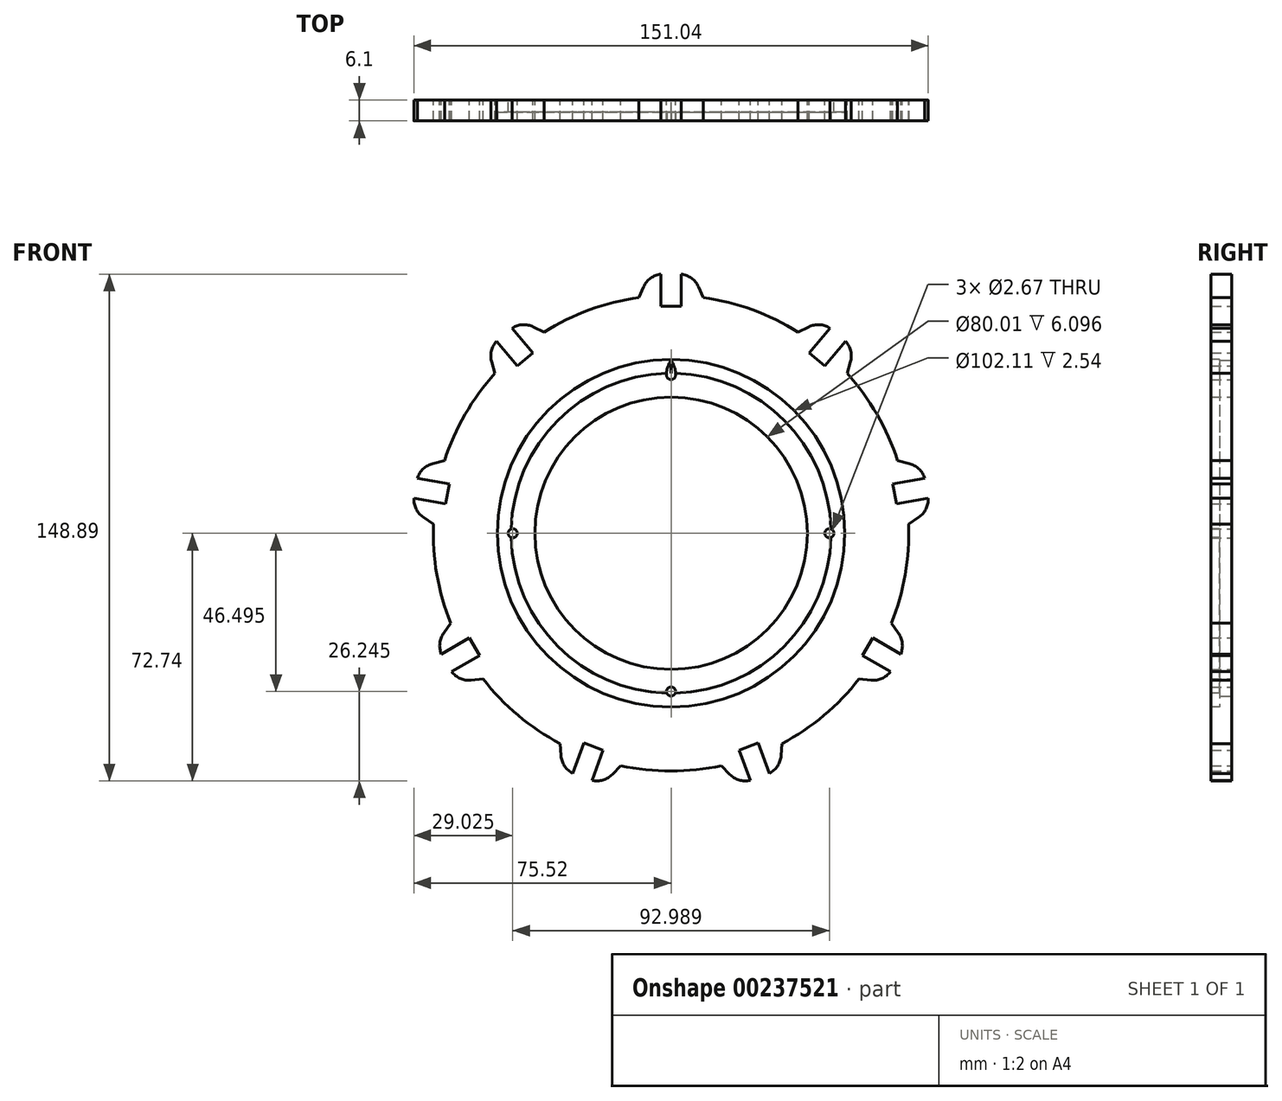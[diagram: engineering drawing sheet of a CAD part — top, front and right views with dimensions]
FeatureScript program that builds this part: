
annotation { "Feature Type Name" : "Feature", "Feature Type Description" : "" }
export const myFeature = defineFeature(function(context is Context, id is Id, definition is map)
    precondition{}
    {
        {
            var Q0;
            Q0=qCreatedBy(makeId("Front.planeOp"),FACE);
            var sketch = newSketch(context, id + "F0", { "sketchPlane" : qUnion([Q0])});
            skCircle(sketch, "E0", {"center": v(0, 0) * mm, "radius": 69.85 * mm});
            skCircle(sketch, "E1", {"center": v(0, 0) * mm, "radius": 40 * mm});
            skCircle(sketch, "E2", {"center": v(0, 0) * mm, "radius": 46.5 * mm, "construction": true});
            skPoint(sketch, "E3.center", {"position": v(0, -7.07) * mm});
            skLineSegment(sketch, "E4", {"start": v(-9.44, 69.2) * mm, "end": v(-8.02, 72.42) * mm});
            skLineSegment(sketch, "E5", {"start": v(-2.21, 76.2) * mm, "end": v(2.21, 76.2) * mm});
            skLineSegment(sketch, "E6", {"start": v(8.02, 72.42) * mm, "end": v(9.44, 69.2) * mm});
            skPoint(sketch, "E7", {"position": v(0, 76.2) * mm});
            skLineSegment(sketch, "E8", {"start": v(-9.44, 69.2) * mm, "end": v(-40, 0) * mm, "construction": true});
            skLineSegment(sketch, "E9", {"start": v(40, 0) * mm, "end": v(9.44, 69.2) * mm, "construction": true});
            skLineSegment(sketch, "E10", {"start": v(-2.98, 76.2) * mm, "end": v(-2.98, 66.67) * mm});
            skLineSegment(sketch, "E11", {"start": v(-2.98, 66.68) * mm, "end": v(2.98, 66.68) * mm});
            skLineSegment(sketch, "E12", {"start": v(2.98, 66.67) * mm, "end": v(2.98, 76.2) * mm});
            skPoint(sketch, "E13", {"position": v(0, 66.67) * mm});
            skPoint(sketch, "E14.visualSharp", {"position": v(-6.35, 76.2) * mm});
            skArc(sketch, "E14.filletArc", {"start": v(-2.21, 76.2) * mm, "mid": v(-5.68, 75.17) * mm, "end": v(-8.02, 72.42) * mm});
            skPoint(sketch, "E15.visualSharp", {"position": v(6.35, 76.2) * mm});
            skArc(sketch, "E15.filletArc", {"start": v(8.02, 72.42) * mm, "mid": v(5.68, 75.17) * mm, "end": v(2.21, 76.2) * mm});
            skCircle(sketch, "E16.MirrorC", {"center": v(0, 46.5) * mm, "radius": 1.33 * mm});
            skCircle(sketch, "E17", {"center": v(0, 0) * mm, "radius": 66.72 * mm, "construction": true});
            skCircle(sketch, "E18.1.0", {"center": v(-46.5, 0) * mm, "radius": 1.33 * mm});
            skCircle(sketch, "E18.2.0", {"center": v(0, -46.5) * mm, "radius": 1.33 * mm});
            skCircle(sketch, "E18.3.0", {"center": v(46.5, 0) * mm, "radius": 1.33 * mm});
            skCircle(sketch, "E19", {"center": v(0, 0) * mm, "radius": 50.8 * mm, "construction": true});
            skArc(sketch, "E20", {"start": v(1.33, 46.48) * mm, "mid": v(1, 48.74) * mm, "end": v(0, 50.8) * mm});
            skArc(sketch, "E21", {"start": v(0, 50.8) * mm, "mid": v(-1, 48.74) * mm, "end": v(-1.33, 46.48) * mm});
            skLineSegment(sketch, "E22.1.0", {"start": v(-51.72, 46.95) * mm, "end": v(-52.7, 50.32) * mm});
            skArc(sketch, "E22.1.1", {"start": v(-50.68, 56.95) * mm, "mid": v(-52.67, 53.93) * mm, "end": v(-52.7, 50.32) * mm});
            skLineSegment(sketch, "E22.1.2", {"start": v(-51.27, 56.45) * mm, "end": v(-45.14, 49.16) * mm});
            skLineSegment(sketch, "E22.1.3", {"start": v(-40.57, 53) * mm, "end": v(-46.7, 60.3) * mm});
            skArc(sketch, "E22.1.4", {"start": v(-40.4, 60.63) * mm, "mid": v(-43.97, 61.23) * mm, "end": v(-47.29, 59.8) * mm});
            skLineSegment(sketch, "E22.1.5", {"start": v(-40.4, 60.63) * mm, "end": v(-37.26, 59.08) * mm});
            skLineSegment(sketch, "E22.1.6", {"start": v(-45.14, 49.16) * mm, "end": v(-40.57, 53) * mm});
            skLineSegment(sketch, "E22.2.0", {"start": v(-69.8, 2.72) * mm, "end": v(-72.7, 4.68) * mm});
            skArc(sketch, "E22.2.1", {"start": v(-75.43, 11.05) * mm, "mid": v(-75.01, 7.46) * mm, "end": v(-72.7, 4.68) * mm});
            skLineSegment(sketch, "E22.2.2", {"start": v(-75.56, 10.3) * mm, "end": v(-66.18, 8.64) * mm});
            skLineSegment(sketch, "E22.2.3", {"start": v(-65.14, 14.52) * mm, "end": v(-74.52, 16.17) * mm});
            skArc(sketch, "E22.2.4", {"start": v(-69.92, 20.47) * mm, "mid": v(-73.04, 18.65) * mm, "end": v(-74.66, 15.41) * mm});
            skLineSegment(sketch, "E22.2.5", {"start": v(-69.92, 20.47) * mm, "end": v(-66.52, 21.31) * mm});
            skLineSegment(sketch, "E22.2.6", {"start": v(-66.18, 8.64) * mm, "end": v(-65.14, 14.52) * mm});
            skLineSegment(sketch, "E22.3.0", {"start": v(-55.22, -42.78) * mm, "end": v(-58.7, -43.15) * mm});
            skArc(sketch, "E22.3.1", {"start": v(-64.88, -40.02) * mm, "mid": v(-62.26, -42.5) * mm, "end": v(-58.7, -43.15) * mm});
            skLineSegment(sketch, "E22.3.2", {"start": v(-64.5, -40.68) * mm, "end": v(-56.25, -35.92) * mm});
            skLineSegment(sketch, "E22.3.3", {"start": v(-59.23, -30.75) * mm, "end": v(-67.48, -35.52) * mm});
            skArc(sketch, "E22.3.4", {"start": v(-66.72, -29.26) * mm, "mid": v(-67.94, -32.67) * mm, "end": v(-67.1, -36.18) * mm});
            skLineSegment(sketch, "E22.3.5", {"start": v(-66.72, -29.26) * mm, "end": v(-64.66, -26.43) * mm});
            skLineSegment(sketch, "E22.3.6", {"start": v(-56.25, -35.92) * mm, "end": v(-59.23, -30.75) * mm});
            skLineSegment(sketch, "E22.4.0", {"start": v(-14.8, -68.26) * mm, "end": v(-17.23, -70.8) * mm});
            skArc(sketch, "E22.4.1", {"start": v(-23.98, -72.36) * mm, "mid": v(-20.37, -72.58) * mm, "end": v(-17.23, -70.8) * mm});
            skLineSegment(sketch, "E22.4.2", {"start": v(-23.26, -72.63) * mm, "end": v(-20, -63.67) * mm});
            skLineSegment(sketch, "E22.4.3", {"start": v(-25.6, -61.63) * mm, "end": v(-28.87, -70.58) * mm});
            skArc(sketch, "E22.4.4", {"start": v(-32.3, -65.3) * mm, "mid": v(-31.05, -68.7) * mm, "end": v(-28.14, -70.85) * mm});
            skLineSegment(sketch, "E22.4.5", {"start": v(-32.3, -65.3) * mm, "end": v(-32.54, -61.8) * mm});
            skLineSegment(sketch, "E22.4.6", {"start": v(-20, -63.67) * mm, "end": v(-25.6, -61.63) * mm});
            skLineSegment(sketch, "E22.5.0", {"start": v(32.54, -61.8) * mm, "end": v(32.3, -65.3) * mm});
            skArc(sketch, "E22.5.1", {"start": v(28.14, -70.85) * mm, "mid": v(31.05, -68.7) * mm, "end": v(32.3, -65.3) * mm});
            skLineSegment(sketch, "E22.5.2", {"start": v(28.87, -70.58) * mm, "end": v(25.6, -61.63) * mm});
            skLineSegment(sketch, "E22.5.3", {"start": v(20, -63.67) * mm, "end": v(23.26, -72.63) * mm});
            skArc(sketch, "E22.5.4", {"start": v(17.23, -70.8) * mm, "mid": v(20.37, -72.58) * mm, "end": v(23.98, -72.36) * mm});
            skLineSegment(sketch, "E22.5.5", {"start": v(17.23, -70.8) * mm, "end": v(14.8, -68.26) * mm});
            skLineSegment(sketch, "E22.5.6", {"start": v(25.6, -61.63) * mm, "end": v(20, -63.67) * mm});
            skLineSegment(sketch, "E22.6.0", {"start": v(64.66, -26.43) * mm, "end": v(66.72, -29.26) * mm});
            skArc(sketch, "E22.6.1", {"start": v(67.1, -36.18) * mm, "mid": v(67.94, -32.67) * mm, "end": v(66.72, -29.26) * mm});
            skLineSegment(sketch, "E22.6.2", {"start": v(67.48, -35.52) * mm, "end": v(59.23, -30.75) * mm});
            skLineSegment(sketch, "E22.6.3", {"start": v(56.25, -35.92) * mm, "end": v(64.5, -40.68) * mm});
            skArc(sketch, "E22.6.4", {"start": v(58.7, -43.15) * mm, "mid": v(62.26, -42.5) * mm, "end": v(64.88, -40.02) * mm});
            skLineSegment(sketch, "E22.6.5", {"start": v(58.7, -43.15) * mm, "end": v(55.22, -42.78) * mm});
            skLineSegment(sketch, "E22.6.6", {"start": v(59.23, -30.75) * mm, "end": v(56.25, -35.92) * mm});
            skLineSegment(sketch, "E22.7.0", {"start": v(66.52, 21.31) * mm, "end": v(69.92, 20.47) * mm});
            skArc(sketch, "E22.7.1", {"start": v(74.66, 15.41) * mm, "mid": v(73.04, 18.65) * mm, "end": v(69.92, 20.47) * mm});
            skLineSegment(sketch, "E22.7.2", {"start": v(74.52, 16.17) * mm, "end": v(65.14, 14.52) * mm});
            skLineSegment(sketch, "E22.7.3", {"start": v(66.18, 8.64) * mm, "end": v(75.56, 10.3) * mm});
            skArc(sketch, "E22.7.4", {"start": v(72.7, 4.68) * mm, "mid": v(75.01, 7.46) * mm, "end": v(75.43, 11.05) * mm});
            skLineSegment(sketch, "E22.7.5", {"start": v(72.7, 4.68) * mm, "end": v(69.8, 2.72) * mm});
            skLineSegment(sketch, "E22.7.6", {"start": v(65.14, 14.52) * mm, "end": v(66.18, 8.64) * mm});
            skLineSegment(sketch, "E22.8.0", {"start": v(37.26, 59.08) * mm, "end": v(40.4, 60.63) * mm});
            skArc(sketch, "E22.8.1", {"start": v(47.29, 59.8) * mm, "mid": v(43.97, 61.23) * mm, "end": v(40.4, 60.63) * mm});
            skLineSegment(sketch, "E22.8.2", {"start": v(46.7, 60.3) * mm, "end": v(40.57, 53) * mm});
            skLineSegment(sketch, "E22.8.3", {"start": v(45.14, 49.16) * mm, "end": v(51.27, 56.45) * mm});
            skArc(sketch, "E22.8.4", {"start": v(52.7, 50.32) * mm, "mid": v(52.67, 53.93) * mm, "end": v(50.68, 56.95) * mm});
            skLineSegment(sketch, "E22.8.5", {"start": v(52.7, 50.32) * mm, "end": v(51.72, 46.95) * mm});
            skLineSegment(sketch, "E22.8.6", {"start": v(40.57, 53) * mm, "end": v(45.14, 49.16) * mm});
            skSolve(sketch);
        }
        {
            var Q0;
            Q0=makeQuery(id+"F0.imprint","IMPRINT",FACE,{"disambiguationData":[TD([[makeQuery(id+"F0.imprint","IMPRINT",EDGE,{"derivedFrom":sQuery(id+"F0.wireOp",EDGE,"E1")}),-1.0]])]});
            var Q1;
            {var subQ0=sQuery(id+"F0.wireOp",EDGE,"E22.1.5");Q1=makeQuery(id+"F0.imprint","IMPRINT",FACE,{"disambiguationData":[TD([[makeQuery(id+"F0.imprint","IMPRINT",EDGE,{"derivedFrom":subQ0}),-1.0]])]});}
            var Q2;
            {var subQ0=sQuery(id+"F0.wireOp",EDGE,"E22.1.0");Q2=makeQuery(id+"F0.imprint","IMPRINT",FACE,{"disambiguationData":[TD([[makeQuery(id+"F0.imprint","IMPRINT",EDGE,{"derivedFrom":subQ0}),-1.0]])]});}
            var Q3;
            {var subQ0=sQuery(id+"F0.wireOp",EDGE,"E4");Q3=makeQuery(id+"F0.imprint","IMPRINT",FACE,{"disambiguationData":[TD([[makeQuery(id+"F0.imprint","IMPRINT",EDGE,{"derivedFrom":subQ0}),-1.0]])]});}
            var Q4;
            {var subQ0=sQuery(id+"F0.wireOp",EDGE,"E6");Q4=makeQuery(id+"F0.imprint","IMPRINT",FACE,{"disambiguationData":[TD([[makeQuery(id+"F0.imprint","IMPRINT",EDGE,{"derivedFrom":subQ0}),-1.0]])]});}
            var Q5;
            {var subQ0=sQuery(id+"F0.wireOp",EDGE,"E22.8.0");Q5=makeQuery(id+"F0.imprint","IMPRINT",FACE,{"disambiguationData":[TD([[makeQuery(id+"F0.imprint","IMPRINT",EDGE,{"derivedFrom":subQ0}),-1.0]])]});}
            var Q6;
            {var subQ0=sQuery(id+"F0.wireOp",EDGE,"E22.8.5");Q6=makeQuery(id+"F0.imprint","IMPRINT",FACE,{"disambiguationData":[TD([[makeQuery(id+"F0.imprint","IMPRINT",EDGE,{"derivedFrom":subQ0}),-1.0]])]});}
            var Q7;
            {var subQ0=sQuery(id+"F0.wireOp",EDGE,"E22.7.0");Q7=makeQuery(id+"F0.imprint","IMPRINT",FACE,{"disambiguationData":[TD([[makeQuery(id+"F0.imprint","IMPRINT",EDGE,{"derivedFrom":subQ0}),-1.0]])]});}
            var Q8;
            {var subQ0=sQuery(id+"F0.wireOp",EDGE,"E22.7.5");Q8=makeQuery(id+"F0.imprint","IMPRINT",FACE,{"disambiguationData":[TD([[makeQuery(id+"F0.imprint","IMPRINT",EDGE,{"derivedFrom":subQ0}),-1.0]])]});}
            var Q9;
            {var subQ0=sQuery(id+"F0.wireOp",EDGE,"E22.6.0");Q9=makeQuery(id+"F0.imprint","IMPRINT",FACE,{"disambiguationData":[TD([[makeQuery(id+"F0.imprint","IMPRINT",EDGE,{"derivedFrom":subQ0}),-1.0]])]});}
            var Q10;
            {var subQ0=sQuery(id+"F0.wireOp",EDGE,"E22.6.5");Q10=makeQuery(id+"F0.imprint","IMPRINT",FACE,{"disambiguationData":[TD([[makeQuery(id+"F0.imprint","IMPRINT",EDGE,{"derivedFrom":subQ0}),-1.0]])]});}
            var Q11;
            {var subQ0=sQuery(id+"F0.wireOp",EDGE,"E22.5.5");Q11=makeQuery(id+"F0.imprint","IMPRINT",FACE,{"disambiguationData":[TD([[makeQuery(id+"F0.imprint","IMPRINT",EDGE,{"derivedFrom":subQ0}),-1.0]])]});}
            var Q12;
            {var subQ0=sQuery(id+"F0.wireOp",EDGE,"E22.5.0");Q12=makeQuery(id+"F0.imprint","IMPRINT",FACE,{"disambiguationData":[TD([[makeQuery(id+"F0.imprint","IMPRINT",EDGE,{"derivedFrom":subQ0}),-1.0]])]});}
            var Q13;
            {var subQ0=sQuery(id+"F0.wireOp",EDGE,"E22.4.5");Q13=makeQuery(id+"F0.imprint","IMPRINT",FACE,{"disambiguationData":[TD([[makeQuery(id+"F0.imprint","IMPRINT",EDGE,{"derivedFrom":subQ0}),-1.0]])]});}
            var Q14;
            {var subQ0=sQuery(id+"F0.wireOp",EDGE,"E22.4.0");Q14=makeQuery(id+"F0.imprint","IMPRINT",FACE,{"disambiguationData":[TD([[makeQuery(id+"F0.imprint","IMPRINT",EDGE,{"derivedFrom":subQ0}),-1.0]])]});}
            var Q15;
            {var subQ0=sQuery(id+"F0.wireOp",EDGE,"E22.3.0");Q15=makeQuery(id+"F0.imprint","IMPRINT",FACE,{"disambiguationData":[TD([[makeQuery(id+"F0.imprint","IMPRINT",EDGE,{"derivedFrom":subQ0}),-1.0]])]});}
            var Q16;
            {var subQ0=sQuery(id+"F0.wireOp",EDGE,"E22.3.5");Q16=makeQuery(id+"F0.imprint","IMPRINT",FACE,{"disambiguationData":[TD([[makeQuery(id+"F0.imprint","IMPRINT",EDGE,{"derivedFrom":subQ0}),-1.0]])]});}
            var Q17;
            {var subQ0=sQuery(id+"F0.wireOp",EDGE,"E22.2.0");Q17=makeQuery(id+"F0.imprint","IMPRINT",FACE,{"disambiguationData":[TD([[makeQuery(id+"F0.imprint","IMPRINT",EDGE,{"derivedFrom":subQ0}),-1.0]])]});}
            var Q18;
            {var subQ0=sQuery(id+"F0.wireOp",EDGE,"E22.2.5");Q18=makeQuery(id+"F0.imprint","IMPRINT",FACE,{"disambiguationData":[TD([[makeQuery(id+"F0.imprint","IMPRINT",EDGE,{"derivedFrom":subQ0}),-1.0]])]});}
            extrude(context, id + "F1", {"entities" : qUnion([Q0, Q1, Q2, Q3, Q4, Q5, Q6, Q7, Q8, Q9, Q10, Q11, Q12, Q13, Q14, Q15, Q16, Q17, Q18]), "offsetDistance" : 25.4 * mm, "depth" : 6.1 * mm});
        }
        {
            var Q0;
            Q0=makeQuery(id+"F1.opExtrude","CAP_FACE",FACE,{"disambiguationData":[OSD([sQuery(id+"F0.wireOp",EDGE,"E0"),sQuery(id+"F0.wireOp",EDGE,"E1"),sQuery(id+"F0.wireOp",EDGE,"s7rXqqL2-3z2l-88EV-UIsY-hwb08Po9ZJjJ"),sQuery(id+"F0.wireOp",EDGE,"E3.1.0"),sQuery(id+"F0.wireOp",EDGE,"E3.2.0"),sQuery(id+"F0.wireOp",EDGE,"E3.3.0"),sQuery(id+"F0.wireOp",EDGE,"E4"),sQuery(id+"F0.wireOp",EDGE,"E6"),sQuery(id+"F0.wireOp",EDGE,"E10"),sQuery(id+"F0.wireOp",EDGE,"E11"),sQuery(id+"F0.wireOp",EDGE,"E12"),sQuery(id+"F0.wireOp",EDGE,"E14.filletArc"),sQuery(id+"F0.wireOp",EDGE,"E15.filletArc"),sQuery(id+"F0.wireOp",EDGE,"e3144966-756d-47fd-8283-5f46bd2110e0.1.0"),sQuery(id+"F0.wireOp",EDGE,"e3144966-756d-47fd-8283-5f46bd2110e0.1.1"),sQuery(id+"F0.wireOp",EDGE,"e3144966-756d-47fd-8283-5f46bd2110e0.1.2"),sQuery(id+"F0.wireOp",EDGE,"e3144966-756d-47fd-8283-5f46bd2110e0.1.3"),sQuery(id+"F0.wireOp",EDGE,"e3144966-756d-47fd-8283-5f46bd2110e0.1.4"),sQuery(id+"F0.wireOp",EDGE,"e3144966-756d-47fd-8283-5f46bd2110e0.1.6"),sQuery(id+"F0.wireOp",EDGE,"e3144966-756d-47fd-8283-5f46bd2110e0.1.7"),sQuery(id+"F0.wireOp",EDGE,"e3144966-756d-47fd-8283-5f46bd2110e0.2.0"),sQuery(id+"F0.wireOp",EDGE,"e3144966-756d-47fd-8283-5f46bd2110e0.2.1"),sQuery(id+"F0.wireOp",EDGE,"e3144966-756d-47fd-8283-5f46bd2110e0.2.2"),sQuery(id+"F0.wireOp",EDGE,"e3144966-756d-47fd-8283-5f46bd2110e0.2.3"),sQuery(id+"F0.wireOp",EDGE,"e3144966-756d-47fd-8283-5f46bd2110e0.2.4"),sQuery(id+"F0.wireOp",EDGE,"e3144966-756d-47fd-8283-5f46bd2110e0.2.6"),sQuery(id+"F0.wireOp",EDGE,"e3144966-756d-47fd-8283-5f46bd2110e0.2.7"),sQuery(id+"F0.wireOp",EDGE,"e3144966-756d-47fd-8283-5f46bd2110e0.3.0"),sQuery(id+"F0.wireOp",EDGE,"e3144966-756d-47fd-8283-5f46bd2110e0.3.1"),sQuery(id+"F0.wireOp",EDGE,"e3144966-756d-47fd-8283-5f46bd2110e0.3.2"),sQuery(id+"F0.wireOp",EDGE,"e3144966-756d-47fd-8283-5f46bd2110e0.3.3"),sQuery(id+"F0.wireOp",EDGE,"e3144966-756d-47fd-8283-5f46bd2110e0.3.4"),sQuery(id+"F0.wireOp",EDGE,"e3144966-756d-47fd-8283-5f46bd2110e0.3.6"),sQuery(id+"F0.wireOp",EDGE,"e3144966-756d-47fd-8283-5f46bd2110e0.3.7"),sQuery(id+"F0.wireOp",EDGE,"e3144966-756d-47fd-8283-5f46bd2110e0.4.0"),sQuery(id+"F0.wireOp",EDGE,"e3144966-756d-47fd-8283-5f46bd2110e0.4.1"),sQuery(id+"F0.wireOp",EDGE,"e3144966-756d-47fd-8283-5f46bd2110e0.4.2"),sQuery(id+"F0.wireOp",EDGE,"e3144966-756d-47fd-8283-5f46bd2110e0.4.3"),sQuery(id+"F0.wireOp",EDGE,"e3144966-756d-47fd-8283-5f46bd2110e0.4.4"),sQuery(id+"F0.wireOp",EDGE,"e3144966-756d-47fd-8283-5f46bd2110e0.4.6"),sQuery(id+"F0.wireOp",EDGE,"e3144966-756d-47fd-8283-5f46bd2110e0.4.7"),sQuery(id+"F0.wireOp",EDGE,"e3144966-756d-47fd-8283-5f46bd2110e0.5.0"),sQuery(id+"F0.wireOp",EDGE,"e3144966-756d-47fd-8283-5f46bd2110e0.5.1"),sQuery(id+"F0.wireOp",EDGE,"e3144966-756d-47fd-8283-5f46bd2110e0.5.2"),sQuery(id+"F0.wireOp",EDGE,"e3144966-756d-47fd-8283-5f46bd2110e0.5.3"),sQuery(id+"F0.wireOp",EDGE,"e3144966-756d-47fd-8283-5f46bd2110e0.5.4"),sQuery(id+"F0.wireOp",EDGE,"e3144966-756d-47fd-8283-5f46bd2110e0.5.6"),sQuery(id+"F0.wireOp",EDGE,"e3144966-756d-47fd-8283-5f46bd2110e0.5.7"),sQuery(id+"F0.wireOp",EDGE,"e3144966-756d-47fd-8283-5f46bd2110e0.6.0"),sQuery(id+"F0.wireOp",EDGE,"e3144966-756d-47fd-8283-5f46bd2110e0.6.1"),sQuery(id+"F0.wireOp",EDGE,"e3144966-756d-47fd-8283-5f46bd2110e0.6.2"),sQuery(id+"F0.wireOp",EDGE,"e3144966-756d-47fd-8283-5f46bd2110e0.6.3"),sQuery(id+"F0.wireOp",EDGE,"e3144966-756d-47fd-8283-5f46bd2110e0.6.4"),sQuery(id+"F0.wireOp",EDGE,"e3144966-756d-47fd-8283-5f46bd2110e0.6.6"),sQuery(id+"F0.wireOp",EDGE,"e3144966-756d-47fd-8283-5f46bd2110e0.6.7"),sQuery(id+"F0.wireOp",EDGE,"e3144966-756d-47fd-8283-5f46bd2110e0.7.0"),sQuery(id+"F0.wireOp",EDGE,"e3144966-756d-47fd-8283-5f46bd2110e0.7.1"),sQuery(id+"F0.wireOp",EDGE,"e3144966-756d-47fd-8283-5f46bd2110e0.7.2"),sQuery(id+"F0.wireOp",EDGE,"e3144966-756d-47fd-8283-5f46bd2110e0.7.3"),sQuery(id+"F0.wireOp",EDGE,"e3144966-756d-47fd-8283-5f46bd2110e0.7.4"),sQuery(id+"F0.wireOp",EDGE,"e3144966-756d-47fd-8283-5f46bd2110e0.7.6"),sQuery(id+"F0.wireOp",EDGE,"e3144966-756d-47fd-8283-5f46bd2110e0.7.7"),sQuery(id+"F0.wireOp",EDGE,"e3144966-756d-47fd-8283-5f46bd2110e0.8.0"),sQuery(id+"F0.wireOp",EDGE,"e3144966-756d-47fd-8283-5f46bd2110e0.8.1"),sQuery(id+"F0.wireOp",EDGE,"e3144966-756d-47fd-8283-5f46bd2110e0.8.2"),sQuery(id+"F0.wireOp",EDGE,"e3144966-756d-47fd-8283-5f46bd2110e0.8.3"),sQuery(id+"F0.wireOp",EDGE,"e3144966-756d-47fd-8283-5f46bd2110e0.8.4"),sQuery(id+"F0.wireOp",EDGE,"e3144966-756d-47fd-8283-5f46bd2110e0.8.6"),sQuery(id+"F0.wireOp",EDGE,"e3144966-756d-47fd-8283-5f46bd2110e0.8.7")])],"isStart":false});
            var sketch = newSketch(context, id + "F2", { "sketchPlane" : qUnion([Q0])});
            skCircle(sketch, "E23", {"center": v(0, 0) * mm, "radius": 47 * mm});
            skCircle(sketch, "E24", {"center": v(0, 0) * mm, "radius": 51.05 * mm});
            skSolve(sketch);
        }
        {
            var Q0;
            Q0=makeQuery(id+"F2.imprint","IMPRINT",FACE,{"disambiguationData":[TD([[makeQuery(id+"F2.imprint","IMPRINT",EDGE,{"derivedFrom":sQuery(id+"F2.wireOp",EDGE,"E24")}),1.0]])]});
            var Q1;
            {var subQ0=sQuery(id+"F2.wireOp",EDGE,"E23");var subQ12=makeQuery(id+"F1.opExtrude","CAP_EDGE",EDGE,{"disambiguationData":[OSD([sQuery(id+"F0.wireOp",EDGE,"E20")])],"isStart":false});var subQ15=makeQuery(id+"F2.imprint","INTERSECT",VERTEX,{"derivedFrom":[subQ12,subQ0]});Q1=makeQuery(id+"F2.imprint","IMPRINT",FACE,{"disambiguationData":[TD([[makeQuery(id+"F2.imprint","IMPRINT",EDGE,{"disambiguationData":[TD([[subQ15,1.0]])],"derivedFrom":subQ0}),-1.0]])]});}
            extrude(context, id + "F3", {"entities" : qUnion([Q0, Q1]), "operationType" : NewBodyOperationType.REMOVE, "oppositeDirection" : true, "depth" : 2.54 * mm});
        }
        {
            var Q0;
            {var subQ0=sQuery(id+"F0.wireOp",EDGE,"E22.4.5");var subQ1=sQuery(id+"F0.wireOp",EDGE,"E22.3.6");var subQ2=sQuery(id+"F0.wireOp",EDGE,"E22.3.4");var subQ3=sQuery(id+"F0.wireOp",EDGE,"E22.4.2");var subQ4=sQuery(id+"F0.wireOp",EDGE,"E22.3.2");var subQ5=sQuery(id+"F0.wireOp",EDGE,"E22.4.4");var subQ6=sQuery(id+"F0.wireOp",EDGE,"E22.3.3");var subQ7=sQuery(id+"F0.wireOp",EDGE,"E22.3.1");var subQ8=sQuery(id+"F0.wireOp",EDGE,"E22.4.0");var subQ9=sQuery(id+"F0.wireOp",EDGE,"E22.2.6");var subQ10=sQuery(id+"F0.wireOp",EDGE,"E22.2.4");var subQ11=sQuery(id+"F0.wireOp",EDGE,"E22.2.2");var subQ12=sQuery(id+"F0.wireOp",EDGE,"E22.2.0");var subQ13=sQuery(id+"F0.wireOp",EDGE,"E22.1.2");var subQ14=sQuery(id+"F0.wireOp",EDGE,"E22.1.6");var subQ15=sQuery(id+"F0.wireOp",EDGE,"E22.5.0");var subQ16=sQuery(id+"F0.wireOp",EDGE,"E0");var subQ17=sQuery(id+"F0.wireOp",EDGE,"E22.6.5");var subQ18=sQuery(id+"F0.wireOp",EDGE,"E22.6.1");var subQ19=sQuery(id+"F0.wireOp",EDGE,"E12");var subQ20=sQuery(id+"F0.wireOp",EDGE,"E22.5.5");var subQ21=sQuery(id+"F0.wireOp",EDGE,"E22.3.0");var subQ22=sQuery(id+"F0.wireOp",EDGE,"E22.7.5");var subQ23=sQuery(id+"F0.wireOp",EDGE,"E22.3.5");var subQ24=sQuery(id+"F0.wireOp",EDGE,"E22.4.3");var subQ25=sQuery(id+"F0.wireOp",EDGE,"E22.8.5");var subQ26=sQuery(id+"F0.wireOp",EDGE,"E22.7.0");var subQ27=sQuery(id+"F0.wireOp",EDGE,"E22.1.1");var subQ28=sQuery(id+"F0.wireOp",EDGE,"E22.8.4");var subQ29=sQuery(id+"F0.wireOp",EDGE,"E14.filletArc");var subQ30=sQuery(id+"F0.wireOp",EDGE,"E22.6.0");var subQ31=sQuery(id+"F0.wireOp",EDGE,"E22.1.3");var subQ32=sQuery(id+"F0.wireOp",EDGE,"E22.8.6");var subQ33=sQuery(id+"F0.wireOp",EDGE,"E6");var subQ34=sQuery(id+"F0.wireOp",EDGE,"E22.8.0");var subQ35=sQuery(id+"F0.wireOp",EDGE,"E22.7.1");var subQ36=sQuery(id+"F0.wireOp",EDGE,"E4");var subQ37=sQuery(id+"F0.wireOp",EDGE,"E22.1.5");var subQ38=sQuery(id+"F0.wireOp",EDGE,"E22.6.4");var subQ39=sQuery(id+"F0.wireOp",EDGE,"E22.5.1");var subQ40=sQuery(id+"F0.wireOp",EDGE,"E22.4.6");var subQ41=sQuery(id+"F0.wireOp",EDGE,"E22.1.0");var subQ42=sQuery(id+"F0.wireOp",EDGE,"E22.2.5");var subQ43=sQuery(id+"F0.wireOp",EDGE,"E10");var subQ44=sQuery(id+"F0.wireOp",EDGE,"E22.6.6");var subQ45=sQuery(id+"F0.wireOp",EDGE,"E11");var subQ46=sQuery(id+"F0.wireOp",EDGE,"E15.filletArc");var subQ47=sQuery(id+"F0.wireOp",EDGE,"E22.2.3");var subQ48=sQuery(id+"F0.wireOp",EDGE,"E22.2.1");var subQ49=sQuery(id+"F0.wireOp",EDGE,"E22.4.1");var subQ50=sQuery(id+"F0.wireOp",EDGE,"E22.1.4");var subQ51=sQuery(id+"F0.wireOp",EDGE,"E22.5.2");var subQ52=sQuery(id+"F0.wireOp",EDGE,"E22.8.3");var subQ53=sQuery(id+"F0.wireOp",EDGE,"E22.5.3");var subQ54=sQuery(id+"F0.wireOp",EDGE,"E22.5.4");var subQ55=sQuery(id+"F0.wireOp",EDGE,"E22.5.6");var subQ56=sQuery(id+"F0.wireOp",EDGE,"E22.6.2");var subQ57=sQuery(id+"F0.wireOp",EDGE,"E22.6.3");var subQ58=sQuery(id+"F0.wireOp",EDGE,"E22.7.2");var subQ59=sQuery(id+"F0.wireOp",EDGE,"E22.7.3");var subQ60=sQuery(id+"F0.wireOp",EDGE,"E22.7.4");var subQ61=sQuery(id+"F0.wireOp",EDGE,"E22.7.6");var subQ62=sQuery(id+"F0.wireOp",EDGE,"E22.8.1");var subQ63=sQuery(id+"F0.wireOp",EDGE,"E22.8.2");Q0=makeQuery(id+"F3.boolean.opBoolean","SPLIT",FACE,{"disambiguationData":[TD([makeQuery(id+"F1.opExtrude","SWEPT_FACE",FACE,{"disambiguationData":[OSD([subQ36])]})])],"derivedFrom":makeQuery(id+"F1.opExtrude","CAP_FACE",FACE,{"disambiguationData":[OSD([subQ16,sQuery(id+"F0.wireOp",EDGE,"E1"),subQ36,subQ33,subQ43,subQ45,subQ19,subQ29,subQ46,sQuery(id+"F0.wireOp",EDGE,"E16.MirrorC"),sQuery(id+"F0.wireOp",EDGE,"E18.1.0"),sQuery(id+"F0.wireOp",EDGE,"E18.2.0"),sQuery(id+"F0.wireOp",EDGE,"E18.3.0"),sQuery(id+"F0.wireOp",EDGE,"E20"),sQuery(id+"F0.wireOp",EDGE,"E21"),subQ41,subQ27,subQ13,subQ31,subQ50,subQ37,subQ14,subQ12,subQ48,subQ11,subQ47,subQ10,subQ42,subQ9,subQ21,subQ7,subQ4,subQ6,subQ2,subQ23,subQ1,subQ8,subQ49,subQ3,subQ24,subQ5,subQ0,subQ40,subQ15,subQ39,subQ51,subQ53,subQ54,subQ20,subQ55,subQ30,subQ18,subQ56,subQ57,subQ38,subQ17,subQ44,subQ26,subQ35,subQ58,subQ59,subQ60,subQ22,subQ61,subQ34,subQ62,subQ63,subQ52,subQ28,subQ25,subQ32])],"isStart":false})});}
            var sketch = newSketch(context, id + "F4", { "sketchPlane" : qUnion([Q0])});
            skLineSegment(sketch, "E25", {"start": v(-0.03, 51.05) * mm, "end": v(-0.03, 46.99) * mm});
            skLineSegment(sketch, "E26", {"start": v(0.03, 51.05) * mm, "end": v(0.03, 46.99) * mm});
            skLineSegment(sketch, "E27", {"start": v(-0.03, 49.02) * mm, "end": v(0.03, 49.02) * mm, "construction": true});
            skPoint(sketch, "E28", {"position": v(0, 49.02) * mm});
            skArc(sketch, "E29", {"start": v(0.03, 51.05) * mm, "mid": v(0, 51.05) * mm, "end": v(-0.03, 51.05) * mm});
            skArc(sketch, "E30", {"start": v(0.03, 46.99) * mm, "mid": v(0, 46.99) * mm, "end": v(-0.03, 46.99) * mm});
            skSolve(sketch);
        }
        {
            var Q0;
            Q0=qSketchRegion(id+"F4",true);
            var Q1;
            Q1=makeQuery(id+"F3.boolean.opBoolean","COPY",FACE,{"derivedFrom":makeQuery(id+"F3.opExtrude","CAP_FACE",FACE,{"disambiguationData":[OSD([sQuery(id+"F0.wireOp",EDGE,"E18.1.0"),sQuery(id+"F0.wireOp",EDGE,"E18.2.0"),sQuery(id+"F0.wireOp",EDGE,"E18.3.0"),sQuery(id+"F0.wireOp",EDGE,"E20"),sQuery(id+"F0.wireOp",EDGE,"E21"),sQuery(id+"F2.wireOp",EDGE,"E23"),sQuery(id+"F2.wireOp",EDGE,"E24")])],"isStart":false})});
            extrude(context, id + "F5", {"entities" : qUnion([Q0]), "operationType" : NewBodyOperationType.ADD, "endBound" : BoundingType.UP_TO_SURFACE, "oppositeDirection" : true, "endBoundEntityFace" : qUnion([Q1]), "depth" : 25.4 * mm});
        }
    });
